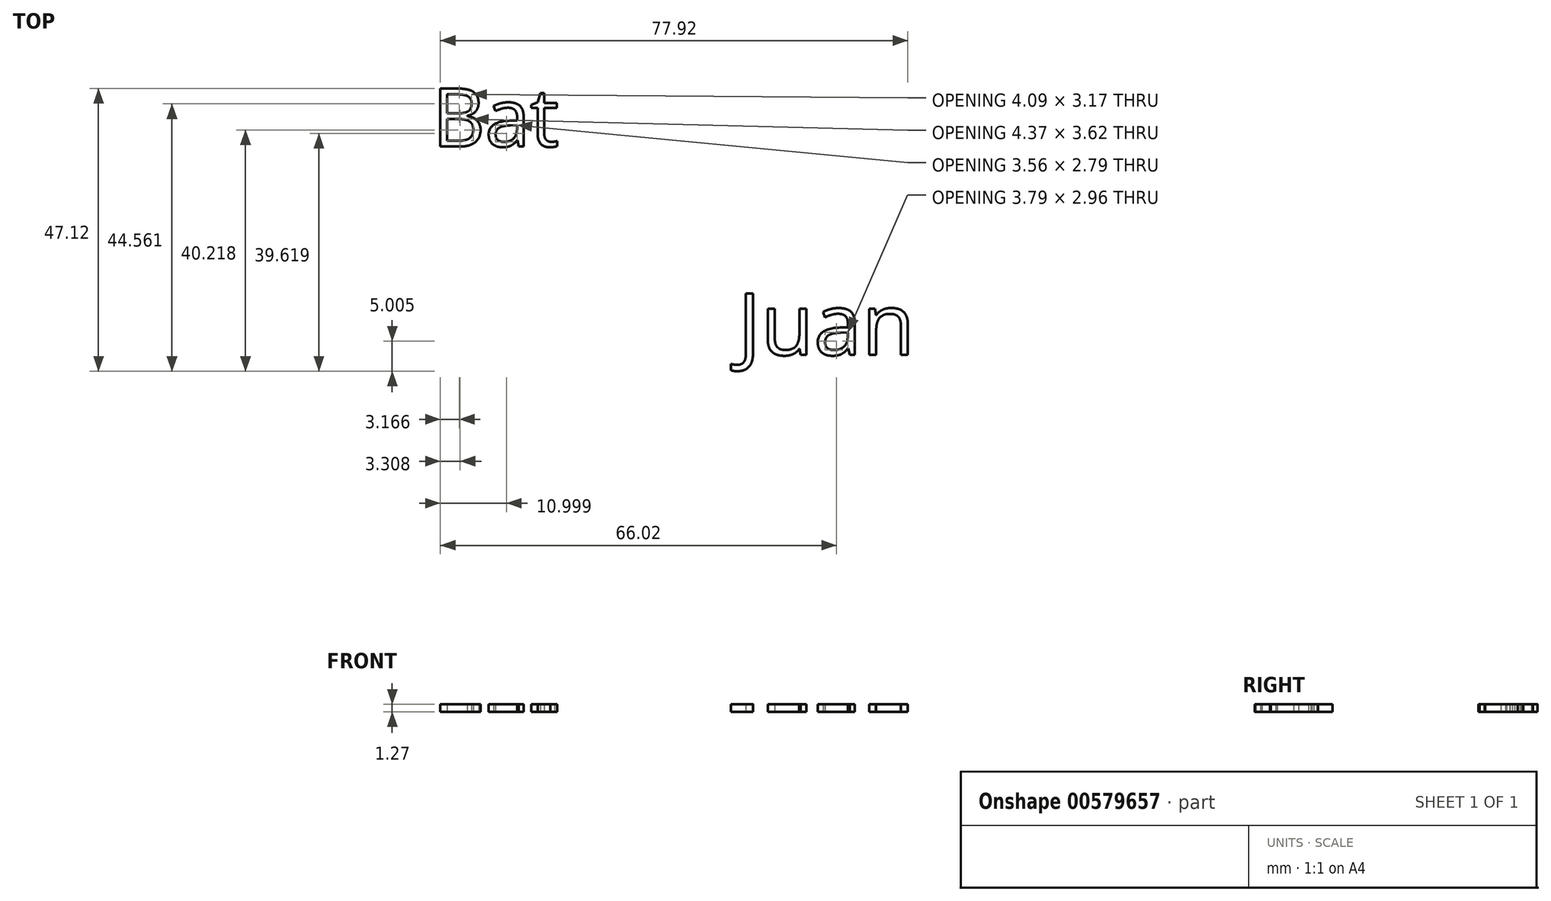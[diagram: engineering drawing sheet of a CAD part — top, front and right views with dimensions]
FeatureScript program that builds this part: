
annotation { "Feature Type Name" : "Feature", "Feature Type Description" : "" }
export const myFeature = defineFeature(function(context is Context, id is Id, definition is map)
    precondition{}
    {
        {
            var Q0;
            Q0=qCreatedBy(makeId("Top.planeOp"),FACE);
            var sketch = newSketch(context, id + "F0", { "sketchPlane" : qUnion([Q0])});
            skText(sketch, "E0", { "text": "Bat\n", "fontName": "OpenSans-Regular.ttf"});
            const initialGuessF0  = {"E0": [-0.07574, 0.06645, 1, 0, 0.00975]};
            skSetInitialGuess(sketch, initialGuessF0);
            skSolve(sketch);
        }
        {
            var Q0;
            Q0=qCreatedBy(makeId("Top.planeOp"),FACE);
            var sketch = newSketch(context, id + "F1", { "sketchPlane" : qUnion([Q0])});
            skText(sketch, "E1", { "text": "Juan\n", "fontName": "OpenSans-Regular.ttf"});
            const initialGuessF1  = {"E1": [-0.02484, 0.0317, 1, 0, 0.01036]};
            skSetInitialGuess(sketch, initialGuessF1);
            skSolve(sketch);
        }
        {
            var Q0;
            Q0 = qSketchRegion(id + "F1", true);
            var Q1;
            Q1 = qSketchRegion(id + "F0", true);
            extrude(context, id + "F2", {"entities" : qUnion([Q0, Q1]), "depth" : 1.27 * mm, "offsetDistance" : 25.4 * mm});
        }
    });
